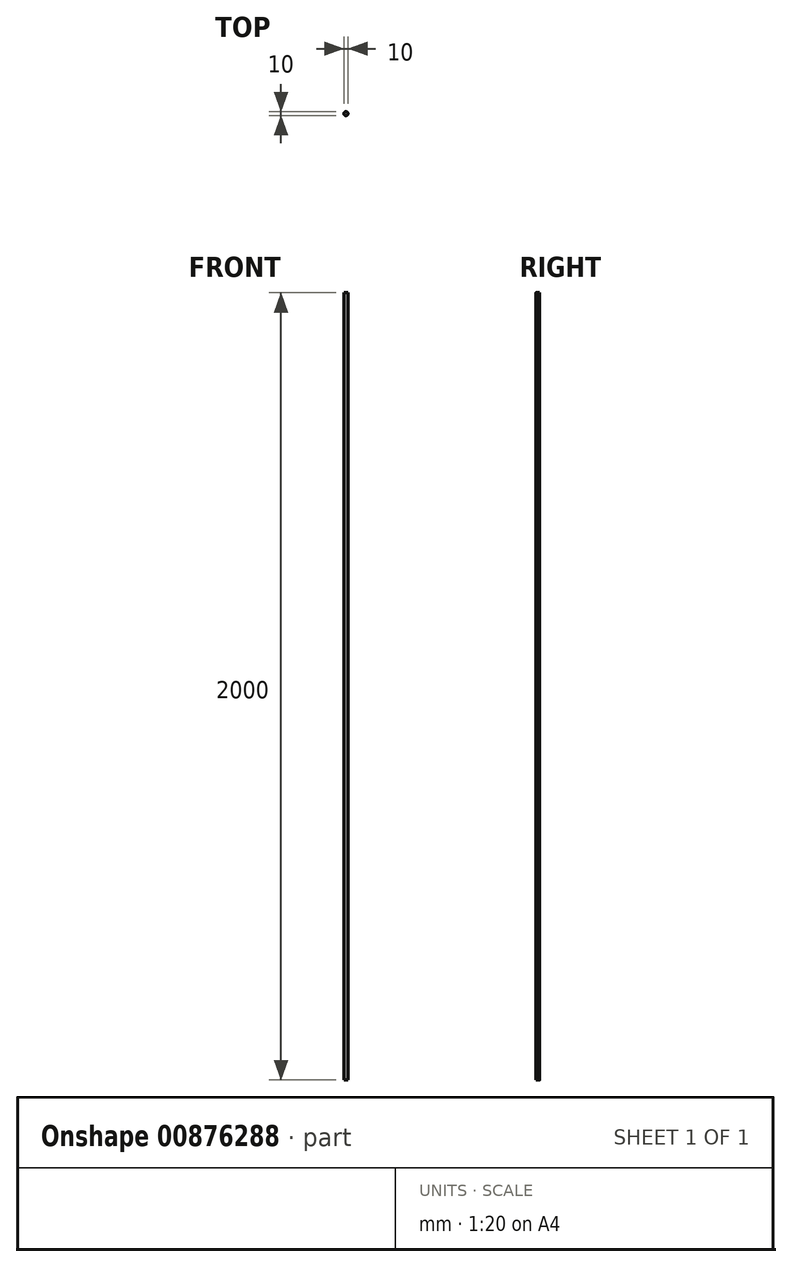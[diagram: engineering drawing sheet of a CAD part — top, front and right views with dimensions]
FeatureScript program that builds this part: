
annotation { "Feature Type Name" : "Feature", "Feature Type Description" : "" }
export const myFeature = defineFeature(function(context is Context, id is Id, definition is map)
    precondition{}
    {
        {
            var Q0;
            Q0=qCreatedBy(makeId("Front.planeOp"),FACE);
            var sketch = newSketch(context, id + "F0", { "sketchPlane" : qUnion([Q0])});
            skLineSegment(sketch, "E0.bottom", {"start": v(0, 675.5) * mm, "end": v(5, 675.5) * mm});
            skLineSegment(sketch, "E0.top", {"start": v(0, -1324.5) * mm, "end": v(5, -1324.5) * mm});
            skLineSegment(sketch, "E0.left", {"start": v(0, 675.5) * mm, "end": v(0, -1324.5) * mm});
            skLineSegment(sketch, "E0.right", {"start": v(5, 675.5) * mm, "end": v(5, -1324.5) * mm});
            skSolve(sketch);
        }
        {
            var Q0;
            Q0=makeQuery(id+"F0.imprint","IMPRINT",FACE,{"disambiguationData":[TD([[makeQuery(id+"F0.imprint","IMPRINT",EDGE,{"derivedFrom":sQuery(id+"F0.wireOp",EDGE,"E0.bottom")}),-1.0]])]});
            var Q1;
            Q1=qSketchRegion(id+"F0",true);
            var Q2;
            Q2=sQuery(id+"F0.wireOp",EDGE,"E0.left");
            revolve(context, id + "F1", {"surfaceOperationType" : NewSurfaceOperationType.NEW, "entities" : qUnion([Q0, Q1]), "axis" : qUnion([Q2]), "revolveType" : RevolveType.FULL});
        }
    });
